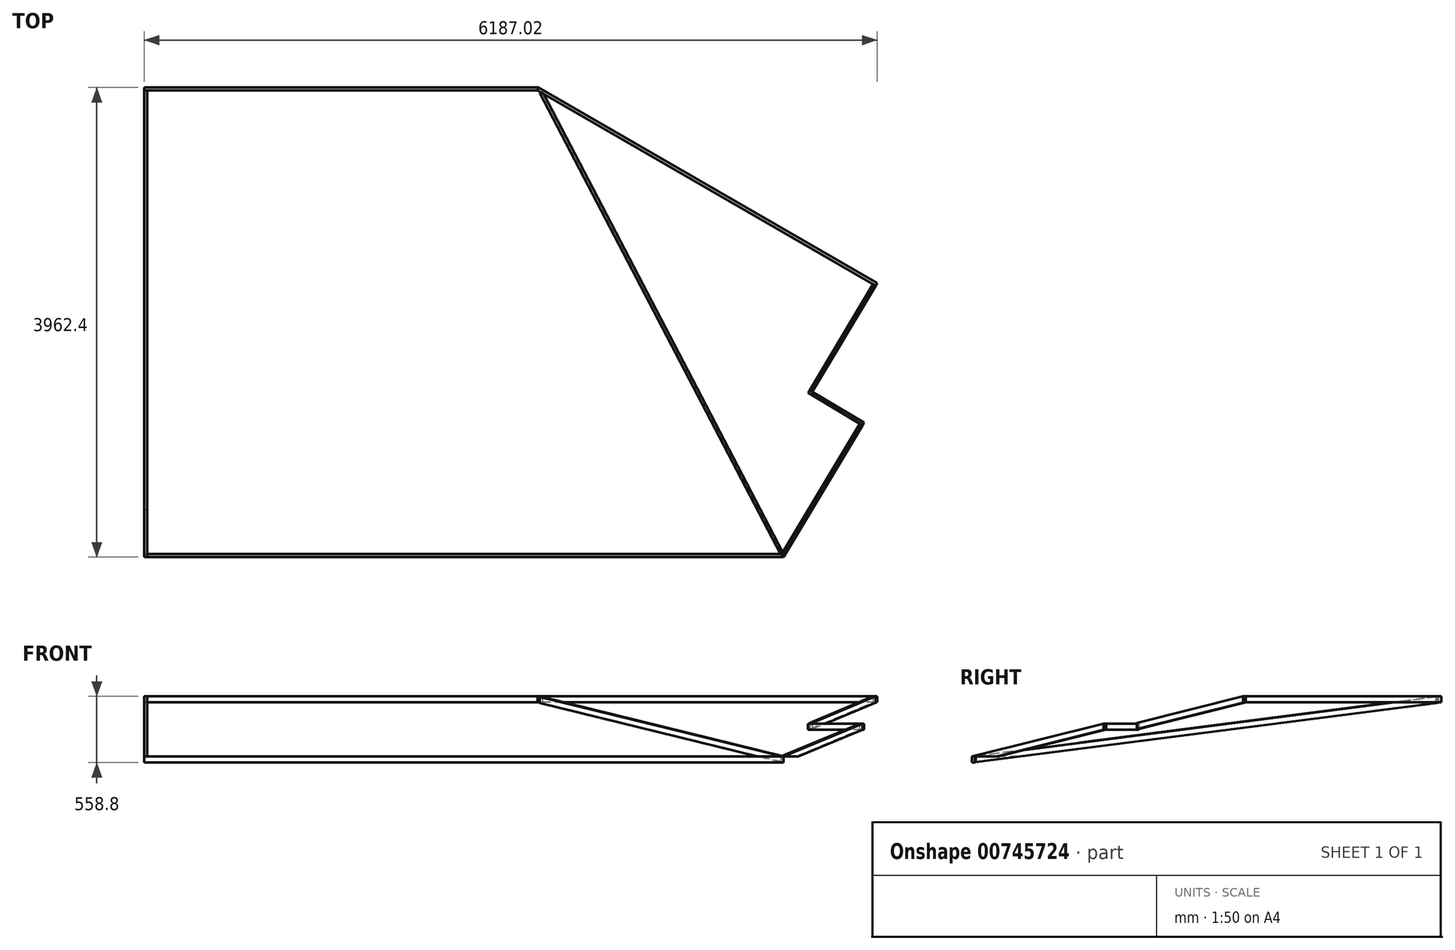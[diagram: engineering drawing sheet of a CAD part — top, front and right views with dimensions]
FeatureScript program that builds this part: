
annotation { "Feature Type Name" : "Feature", "Feature Type Description" : "" }
export const myFeature = defineFeature(function(context is Context, id is Id, definition is map)
    precondition{}
    {
        {
            var Q0;
            Q0=qCreatedBy(makeId("Top.planeOp"),FACE);
            var sketch = newSketch(context, id + "F0", { "sketchPlane" : qUnion([Q0])});
            skLineSegment(sketch, "E0", {"start": v(0, 0) * mm, "end": v(3327.4, 0) * mm});
            skLineSegment(sketch, "E1", {"start": v(3327.4, 0) * mm, "end": v(6187.02, -1651) * mm});
            skLineSegment(sketch, "E2", {"start": v(6173.98, -1672.8) * mm, "end": v(3320.6, -25.4) * mm});
            skLineSegment(sketch, "E3", {"start": v(3320.6, -25.4) * mm, "end": v(0, -25.4) * mm});
            skLineSegment(sketch, "E4", {"start": v(0, -25.4) * mm, "end": v(0, 0) * mm});
            skLineSegment(sketch, "E5", {"start": v(3327.4, 0) * mm, "end": v(3320.6, -25.4) * mm});
            skLineSegment(sketch, "E6", {"start": v(6187.02, -1651) * mm, "end": v(6173.98, -1672.8) * mm});
            skSolve(sketch);
        }
        {
            var Q0;
            Q0=makeQuery(id+"F0.imprint","IMPRINT",FACE,{"disambiguationData":[TD([[makeQuery(id+"F0.imprint","IMPRINT",EDGE,{"derivedFrom":sQuery(id+"F0.wireOp",EDGE,"E0")}),-1.0]])]});
            extrude(context, id + "F1", {"entities" : qUnion([Q0]), "oppositeDirection" : true, "depth" : 50.8 * mm, "offsetDistance" : 25.4 * mm});
        }
        {
            var Q0;
            Q0=makeQuery(id+"F0.imprint","IMPRINT",FACE,{"disambiguationData":[TD([[makeQuery(id+"F0.imprint","IMPRINT",EDGE,{"derivedFrom":sQuery(id+"F0.wireOp",EDGE,"E1")}),-1.0]])]});
            extrude(context, id + "F2", {"entities" : qUnion([Q0]), "oppositeDirection" : true, "depth" : 50.8 * mm, "offsetDistance" : 25.4 * mm});
        }
        {
            var Q0;
            Q0=qCreatedBy(makeId("Right.planeOp"),FACE);
            var sketch = newSketch(context, id + "F3", { "sketchPlane" : qUnion([Q0])});
            skLineSegment(sketch, "E7", {"start": v(-25.4, 0) * mm, "end": v(-3962.4, -508) * mm});
            skLineSegment(sketch, "E8", {"start": v(-3962.4, -508) * mm, "end": v(-3962.4, -558.8) * mm, "construction": true});
            skLineSegment(sketch, "E9", {"start": v(-3962.4, -558.8) * mm, "end": v(0, -558.8) * mm, "construction": true});
            skLineSegment(sketch, "E10", {"start": v(0, -558.8) * mm, "end": v(0, -50.8) * mm, "construction": true});
            skLineSegment(sketch, "E11", {"start": v(0, -50.8) * mm, "end": v(-25.4, -50.8) * mm});
            skLineSegment(sketch, "E12", {"start": v(-25.4, -50.8) * mm, "end": v(-25.4, -508) * mm, "construction": true});
            skLineSegment(sketch, "E13", {"start": v(0, -508) * mm, "end": v(-3962.4, -508) * mm, "construction": true});
            skLineSegment(sketch, "E14", {"start": v(-3937, -508) * mm, "end": v(-3937, -558.8) * mm, "construction": true});
            skLineSegment(sketch, "E15", {"start": v(-25.4, -51.22) * mm, "end": v(-3565.44, -508) * mm});
            skLineSegment(sketch, "E16", {"start": v(-25.4, 0) * mm, "end": v(-25.4, -51.22) * mm});
            skLineSegment(sketch, "E17", {"start": v(-3565.44, -508) * mm, "end": v(-3962.4, -508) * mm});
            skLineSegment(sketch, "E18", {"start": v(-3937, -558.8) * mm, "end": v(-3962.4, -558.8) * mm, "construction": true});
            skSolve(sketch);
        }
        {
            var Q0;
            {var subQ3=sQuery(id+"F3.wireOp",EDGE,"E7");Q0=makeQuery(id+"F3.imprint","IMPRINT",FACE,{"disambiguationData":[TD([[makeQuery(id+"F3.imprint","IMPRINT",EDGE,{"derivedFrom":subQ3}),1.0]])]});}
            extrude(context, id + "F4", {"entities" : qUnion([Q0]), "depth" : 25.4 * mm, "offsetDistance" : 25.4 * mm});
        }
        {
            var Q0;
            Q0=makeQuery(id+"F2.opExtrude","SWEPT_FACE",FACE,{"disambiguationData":[OSD([sQuery(id+"F0.wireOp",EDGE,"E6")])]});
            var sketch = newSketch(context, id + "F5", { "sketchPlane" : qUnion([Q0])});
            skLineSegment(sketch, "E19", {"start": v(1732, 0) * mm, "end": v(-630.2, -508) * mm, "construction": true});
            skLineSegment(sketch, "E20", {"start": v(1732, 0) * mm, "end": v(690.6, -223.96) * mm});
            skLineSegment(sketch, "E21", {"start": v(690.6, -223.96) * mm, "end": v(690.6, -275.92) * mm});
            skLineSegment(sketch, "E22", {"start": v(690.6, -275.92) * mm, "end": v(1732, -51.96) * mm});
            skLineSegment(sketch, "E23", {"start": v(1732, 0) * mm, "end": v(1732, -51.96) * mm});
            skLineSegment(sketch, "E24", {"start": v(665.2, -229.42) * mm, "end": v(690.6, -229.42) * mm});
            skLineSegment(sketch, "E25", {"start": v(690.6, -229.42) * mm, "end": v(690.6, -280.22) * mm});
            skLineSegment(sketch, "E26", {"start": v(690.6, -280.22) * mm, "end": v(665.2, -280.22) * mm});
            skLineSegment(sketch, "E27", {"start": v(665.2, -280.22) * mm, "end": v(665.2, -229.42) * mm});
            skSolve(sketch);
        }
        {
            var Q0;
            {var subQ1=sQuery(id+"F5.wireOp",EDGE,"E20");Q0=makeQuery(id+"F5.imprint","IMPRINT",FACE,{"disambiguationData":[TD([[makeQuery(id+"F5.imprint","IMPRINT",EDGE,{"derivedFrom":subQ1}),1.0]])]});}
            extrude(context, id + "F6", {"entities" : qUnion([Q0]), "oppositeDirection" : true, "depth" : 25.4 * mm, "offsetDistance" : 25.4 * mm});
        }
        {
            var Q0;
            {var subQ3=sQuery(id+"F5.wireOp",EDGE,"E24");Q0=makeQuery(id+"F5.imprint","IMPRINT",FACE,{"disambiguationData":[TD([[makeQuery(id+"F5.imprint","IMPRINT",EDGE,{"derivedFrom":subQ3}),-1.0]])]});}
            extrude(context, id + "F7", {"entities" : qUnion([Q0]), "depth" : 508 * mm, "offsetDistance" : 25.4 * mm, "hasSecondDirection" : true, "secondDirectionOppositeDirection" : true, "secondDirectionDepth" : 25.4 * mm});
        }
        {
            var Q0;
            Q0=makeQuery(id+"F7.opExtrude","CAP_FACE",FACE,{"disambiguationData":[OSD([sQuery(id+"F5.wireOp",EDGE,"E24"),sQuery(id+"F5.wireOp",EDGE,"E25"),sQuery(id+"F5.wireOp",EDGE,"E26"),sQuery(id+"F5.wireOp",EDGE,"E27")])],"isStart":false});
            var sketch = newSketch(context, id + "F8", { "sketchPlane" : qUnion([Q0])});
            skLineSegment(sketch, "E28", {"start": v(665.2, -229.42) * mm, "end": v(-630.2, -508) * mm});
            skLineSegment(sketch, "E29", {"start": v(-630.2, -508) * mm, "end": v(-388.58, -508) * mm});
            skLineSegment(sketch, "E30", {"start": v(-388.58, -508) * mm, "end": v(665.2, -281.38) * mm});
            skLineSegment(sketch, "E31", {"start": v(665.2, -229.42) * mm, "end": v(665.2, -281.38) * mm});
            skSolve(sketch);
        }
        {
            var Q0;
            Q0 = qSketchRegion(id + "F8", true);
            extrude(context, id + "F9", {"entities" : qUnion([Q0]), "oppositeDirection" : true, "depth" : 25.4 * mm, "offsetDistance" : 25.4 * mm});
        }
        {
            var Q0;
            Q0=makeQuery(id+"F4.opExtrude","SWEPT_FACE",FACE,{"disambiguationData":[OSD([sQuery(id+"F3.wireOp",EDGE,"E17")])]});
            var sketch = newSketch(context, id + "F10", { "sketchPlane" : qUnion([Q0])});
            skLineSegment(sketch, "E32.bottom", {"start": v(0, 3962.4) * mm, "end": v(5398, 3962.4) * mm});
            skLineSegment(sketch, "E32.top", {"start": v(0, 3937) * mm, "end": v(5398, 3937) * mm});
            skLineSegment(sketch, "E32.left", {"start": v(0, 3962.4) * mm, "end": v(0, 3937) * mm});
            skLineSegment(sketch, "E32.right", {"start": v(5398, 3962.4) * mm, "end": v(5398, 3937) * mm});
            skSolve(sketch);
        }
        {
            var Q0;
            Q0 = qSketchRegion(id + "F10", true);
            extrude(context, id + "F11", {"entities" : qUnion([Q0]), "depth" : 50.8 * mm, "offsetDistance" : 25.4 * mm});
        }
        {
            var Q0;
            Q0=makeQuery(id+"F11.opExtrude","CAP_VERTEX",VERTEX,{"disambiguationData":[OSD([sQuery(id+"F10.wireOp",EDGE,"E32.bottom"),sQuery(id+"F10.wireOp",EDGE,"E32.right")])],"isStart":true});
            var Q1;
            Q1=sQuery(id+"F0.wireOp",VERTEX,"E5.start");
            var Q2;
            Q2=makeQuery(id+"F1.opExtrude","CAP_VERTEX",VERTEX,{"disambiguationData":[OSD([sQuery(id+"F0.wireOp",EDGE,"E0"),sQuery(id+"F0.wireOp",EDGE,"E1"),sQuery(id+"F0.wireOp",EDGE,"E5")])],"isStart":false});
            cPlane(context, id + "F12", {"entities" : qUnion([Q0, Q1, Q2]), "cplaneType" : CPlaneType.THREE_POINT, "offset" : 25.4 * mm, "width" : 152.4 * mm, "height" : 152.4 * mm});
        }
        {
            var Q0;
            Q0=qCreatedBy(id+"F12.planeOp",FACE);
            var sketch = newSketch(context, id + "F13", { "sketchPlane" : qUnion([Q0])});
            skLineSegment(sketch, "E33", {"start": v(-5983.18, -555.87) * mm, "end": v(-1588.43, -56.51) * mm});
            skLineSegment(sketch, "E34", {"start": v(-1588.43, -5.38) * mm, "end": v(-1588.43, -56.51) * mm});
            skLineSegment(sketch, "E35", {"start": v(-1588.43, -5.38) * mm, "end": v(-5983.18, -504.74) * mm});
            skLineSegment(sketch, "E36", {"start": v(-5983.18, -504.74) * mm, "end": v(-5983.18, -555.87) * mm});
            skSolve(sketch);
        }
        {
            var Q0;
            Q0 = qSketchRegion(id + "F13", true);
            extrude(context, id + "F14", {"entities" : qUnion([Q0]), "depth" : 12.7 * mm, "offsetDistance" : 25.4 * mm, "hasSecondDirection" : true, "secondDirectionOppositeDirection" : true, "secondDirectionDepth" : 12.7 * mm});
        }
    });
